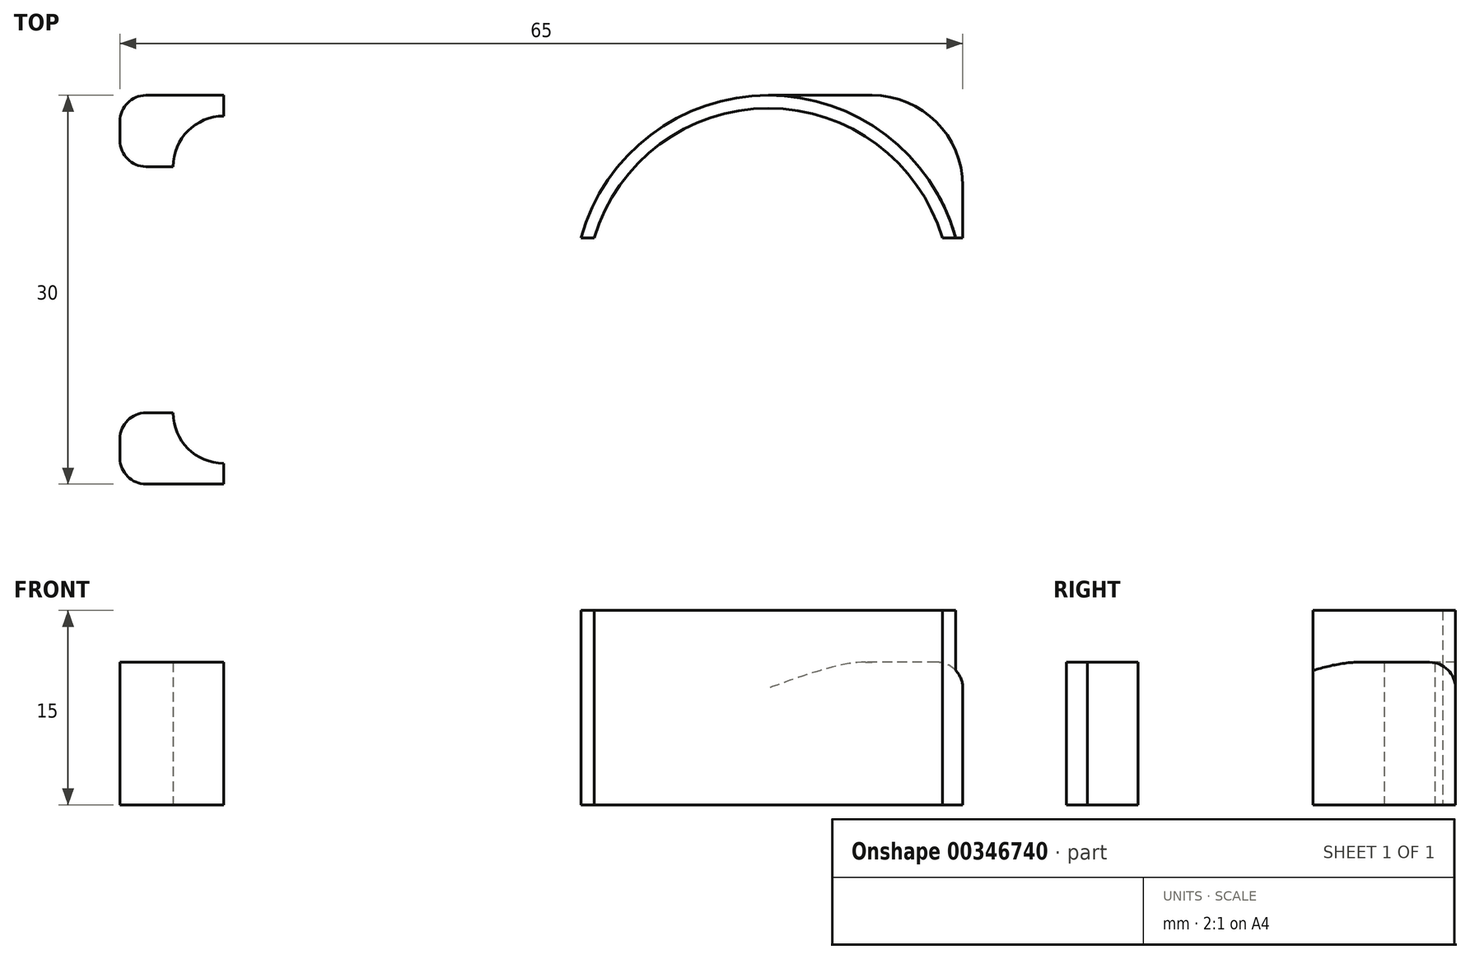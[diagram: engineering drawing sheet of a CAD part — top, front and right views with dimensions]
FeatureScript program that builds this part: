
annotation { "Feature Type Name" : "Feature", "Feature Type Description" : "" }
export const myFeature = defineFeature(function(context is Context, id is Id, definition is map)
    precondition{}
    {
        {
            var Q0;
            Q0=qCreatedBy(makeId("Top.planeOp"),FACE);
            var sketch = newSketch(context, id + "F0", { "sketchPlane" : qUnion([Q0])});
            skLineSegment(sketch, "E0.bottom", {"start": v(0, 0) * mm, "end": v(65, 0) * mm});
            skLineSegment(sketch, "E0.top", {"start": v(0, -11) * mm, "end": v(65, -11) * mm});
            skLineSegment(sketch, "E0.left", {"start": v(0, 0) * mm, "end": v(0, -11) * mm});
            skLineSegment(sketch, "E0.right", {"start": v(65, 0) * mm, "end": v(65, -11) * mm});
            skLineSegment(sketch, "E1.bottom", {"start": v(0, 0) * mm, "end": v(8, 0) * mm});
            skLineSegment(sketch, "E1.top", {"start": v(0, -5.5) * mm, "end": v(8, -5.5) * mm});
            skLineSegment(sketch, "E1.left", {"start": v(0, 0) * mm, "end": v(0, -5.5) * mm});
            skLineSegment(sketch, "E1.right", {"start": v(8, 0) * mm, "end": v(8, -5.5) * mm});
            skCircle(sketch, "E2", {"center": v(8, -5.5) * mm, "radius": 3.9 * mm});
            skLineSegment(sketch, "E3", {"start": v(0, 0) * mm, "end": v(50, 0) * mm});
            skLineSegment(sketch, "E4", {"start": v(50, 0) * mm, "end": v(50, -15) * mm});
            skCircle(sketch, "E5", {"center": v(50, -15) * mm, "radius": 15 * mm});
            skCircle(sketch, "E6", {"center": v(50, -15) * mm, "radius": 14 * mm});
            skSolve(sketch);
        }
        {
            var Q0;
            {var subQ5=sQuery(id+"F0.wireOp",EDGE,"E1.left");Q0=makeQuery(id+"F0.imprint","IMPRINT",FACE,{"disambiguationData":[TD([[makeQuery(id+"F0.imprint","IMPRINT",EDGE,{"derivedFrom":subQ5}),1.0]])]});}
            var Q1;
            {var subQ1=sQuery(id+"F0.wireOp",EDGE,"E0.left");Q1=makeQuery(id+"F0.imprint","IMPRINT",FACE,{"disambiguationData":[TD([[makeQuery(id+"F0.imprint","IMPRINT",EDGE,{"derivedFrom":subQ1}),1.0]])]});}
            extrude(context, id + "F1", {"entities" : qUnion([Q0, Q1]), "depth" : 11 * mm});
        }
        {
            var Q0;
            {var subQ0=sQuery(id+"F0.wireOp",EDGE,"E5");var subQ1=sQuery(id+"F0.wireOp",EDGE,"E0.top");var subQ2=makeQuery(id+"F0.imprint","INTERSECT",VERTEX,{"disambiguationData":[OD(0.0)],"derivedFrom":[subQ1,subQ0]});Q0=makeQuery(id+"F0.imprint","IMPRINT",FACE,{"disambiguationData":[TD([[makeQuery(id+"F0.imprint","IMPRINT",EDGE,{"disambiguationData":[TD([[subQ2,-1.0]])],"derivedFrom":subQ1}),1.0]])]});}
            var Q1;
            {var subQ0=sQuery(id+"F0.wireOp",EDGE,"E5");var subQ1=sQuery(id+"F0.wireOp",EDGE,"E0.top");var subQ2=makeQuery(id+"F0.imprint","INTERSECT",VERTEX,{"disambiguationData":[OD(1.0)],"derivedFrom":[subQ1,subQ0]});Q1=makeQuery(id+"F0.imprint","IMPRINT",FACE,{"disambiguationData":[TD([[makeQuery(id+"F0.imprint","IMPRINT",EDGE,{"disambiguationData":[TD([[subQ2,1.0]])],"derivedFrom":subQ1}),1.0]])]});}
            extrude(context, id + "F2", {"entities" : qUnion([Q0, Q1]), "operationType" : NewBodyOperationType.ADD, "depth" : 15 * mm});
        }
        {
            var Q0;
            Q0=qCreatedBy(makeId("Front.planeOp"),FACE);
            cPlane(context, id + "F3", {"entities" : qUnion([Q0]), "cplaneType" : CPlaneType.OFFSET, "offset" : 15 * mm, "width" : 150 * mm, "height" : 150 * mm});
        }
        {
            var Q0;
            Q0=makeQuery(id+"F1.opExtrude","SWEPT_EDGE",EDGE,{"disambiguationData":[OSD([sQuery(id+"F0.wireOp",EDGE,"E1.left"),sQuery(id+"F0.wireOp",EDGE,"E3")])]});
            var Q1;
            Q1=makeQuery(id+"F1.opExtrude","SWEPT_EDGE",EDGE,{"disambiguationData":[OSD([sQuery(id+"F0.wireOp",EDGE,"E0.top"),sQuery(id+"F0.wireOp",EDGE,"E0.left")])]});
            var Q2;
            Q2=makeQuery(id+"FJc5OMgt0sz76j7_1.opPattern","COPY",EDGE,{"derivedFrom":makeQuery(id+"F1.opExtrude","SWEPT_EDGE",EDGE,{"disambiguationData":[OSD([sQuery(id+"F0.wireOp",EDGE,"E0.top"),sQuery(id+"F0.wireOp",EDGE,"E0.left")])]}),"instanceName":"1"});
            var Q3;
            Q3=makeQuery(id+"FJc5OMgt0sz76j7_1.opPattern","COPY",EDGE,{"derivedFrom":makeQuery(id+"F1.opExtrude","SWEPT_EDGE",EDGE,{"disambiguationData":[OSD([sQuery(id+"F0.wireOp",EDGE,"E1.left"),sQuery(id+"F0.wireOp",EDGE,"E3")])]}),"instanceName":"1"});
            var Q4;
            Q4=makeQuery(id+"FJc5OMgt0sz76j7_1.opPattern","COPY",EDGE,{"derivedFrom":makeQuery(id+"F1.opExtrude","CAP_EDGE",EDGE,{"disambiguationData":[OSD([sQuery(id+"F0.wireOp",EDGE,"E3")])],"isStart":false}),"instanceName":"1"});
            var Q5;
            Q5=makeQuery(id+"FJc5OMgt0sz76j7_1.opPattern","COPY",EDGE,{"derivedFrom":makeQuery(id+"F1.opExtrude","CAP_EDGE",EDGE,{"disambiguationData":[OSD([sQuery(id+"F0.wireOp",EDGE,"E0.top")])],"isStart":false}),"instanceName":"1"});
            var Q6;
            Q6=makeQuery(id+"F1.opExtrude","CAP_EDGE",EDGE,{"disambiguationData":[OSD([sQuery(id+"F0.wireOp",EDGE,"E3")])],"isStart":false});
            var Q7;
            Q7=makeQuery(id+"F1.opExtrude","CAP_EDGE",EDGE,{"disambiguationData":[OSD([sQuery(id+"F0.wireOp",EDGE,"E0.top")])],"isStart":false});
            fillet(context, id + "F4", {"entities" : qUnion([Q0, Q1, Q2, Q3, Q4, Q5, Q6, Q7]), "radius" : 2 * mm, "tangentPropagation" : true, "allowEdgeOverflow" : false});
        }
        {
            var Q0;
            {var subQ0=sQuery(id+"F0.wireOp",EDGE,"E0.bottom");Q0=makeQuery(id+"F0.imprint","IMPRINT",FACE,{"disambiguationData":[TD([[makeQuery(id+"F0.imprint","IMPRINT",EDGE,{"derivedFrom":subQ0}),-1.0]])]});}
            extrude(context, id + "F5", {"entities" : qUnion([Q0]), "operationType" : NewBodyOperationType.ADD, "depth" : 11 * mm});
        }
        {
            var Q0;
            Q0=makeQuery(id+"F5.opExtrude","CAP_EDGE",EDGE,{"disambiguationData":[OSD([sQuery(id+"F0.wireOp",EDGE,"E0.bottom")])],"isStart":false});
            var Q1;
            Q1=makeQuery(id+"F5.opExtrude","CAP_EDGE",EDGE,{"disambiguationData":[OSD([sQuery(id+"F0.wireOp",EDGE,"E0.right")])],"isStart":false});
            fillet(context, id + "F6", {"entities" : qUnion([Q0, Q1]), "radius" : 2 * mm, "tangentPropagation" : true, "allowEdgeOverflow" : false});
        }
        {
            var Q0;
            Q0=makeQuery(id+"F5.opExtrude","SWEPT_EDGE",EDGE,{"disambiguationData":[OSD([sQuery(id+"F0.wireOp",EDGE,"E0.bottom"),sQuery(id+"F0.wireOp",EDGE,"E0.right")])]});
            fillet(context, id + "F7", {"entities" : qUnion([Q0]), "radius" : 7 * mm, "tangentPropagation" : true, "allowEdgeOverflow" : false});
        }
        {
            var Q0;
            Q0=makeQuery(id+"F1.opExtrude","SWEPT_BODY",BODY,{"disambiguationData":[OSD([sQuery(id+"F0.wireOp",EDGE,"E0.top"),sQuery(id+"F0.wireOp",EDGE,"E0.left"),sQuery(id+"F0.wireOp",EDGE,"E1.left"),sQuery(id+"F0.wireOp",EDGE,"E2"),sQuery(id+"F0.wireOp",EDGE,"E3"),sQuery(id+"F0.wireOp",EDGE,"E5")])]});
            var Q1;
            Q1=qCreatedBy(id+"F3.planeOp",FACE);
            mirror(context, id + "F8", {"operationType" : NewBodyOperationType.ADD, "entities" : qUnion([Q0]), "mirrorPlane" : qUnion([Q1])});
        }
    });
